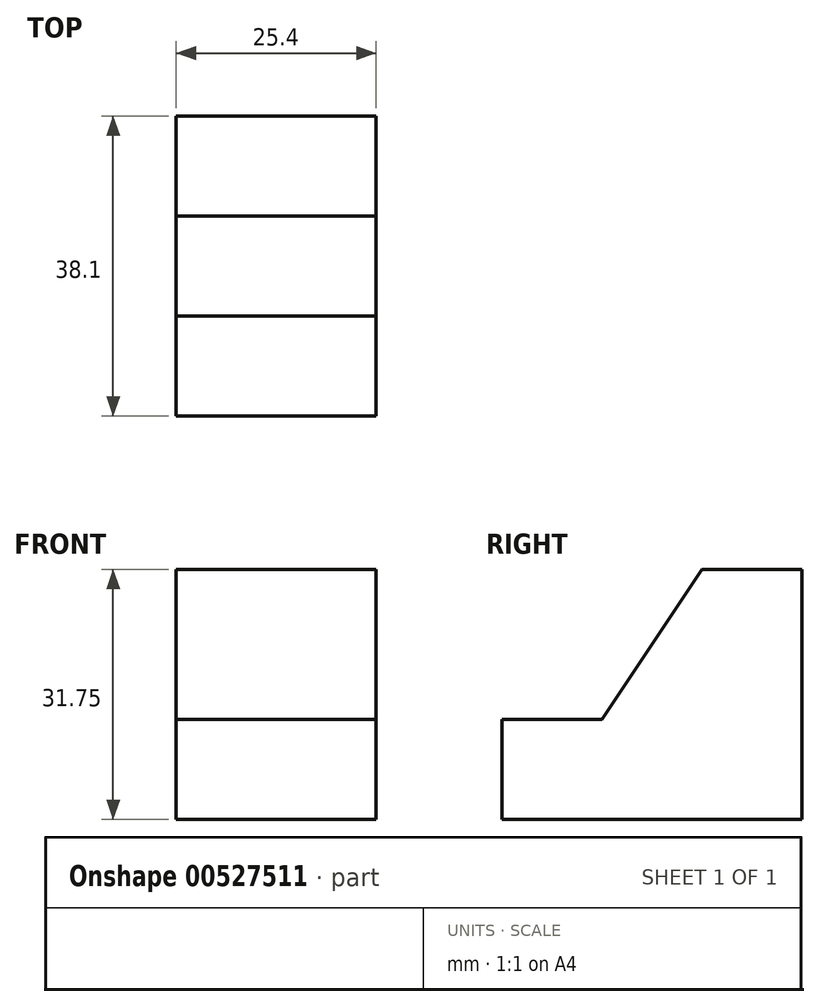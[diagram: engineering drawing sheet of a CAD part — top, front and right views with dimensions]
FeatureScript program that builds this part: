
annotation { "Feature Type Name" : "Feature", "Feature Type Description" : "" }
export const myFeature = defineFeature(function(context is Context, id is Id, definition is map)
    precondition{}
    {
        {
            var Q0;
            Q0=qCreatedBy(makeId("Right.planeOp"),FACE);
            var sketch = newSketch(context, id + "F0", { "sketchPlane" : qUnion([Q0])});
            skLineSegment(sketch, "E0", {"start": v(0, 0) * mm, "end": v(0, 31.75) * mm});
            skLineSegment(sketch, "E1", {"start": v(0, 31.75) * mm, "end": v(-12.7, 31.75) * mm});
            skLineSegment(sketch, "E2", {"start": v(0, 0) * mm, "end": v(-38.1, 0) * mm});
            skLineSegment(sketch, "E3", {"start": v(-38.1, 0) * mm, "end": v(-38.1, 12.7) * mm});
            skLineSegment(sketch, "E4", {"start": v(-38.1, 12.7) * mm, "end": v(-25.4, 12.7) * mm});
            skLineSegment(sketch, "E5", {"start": v(-25.4, 12.7) * mm, "end": v(-12.7, 31.75) * mm});
            skSolve(sketch);
        }
        {
            var Q0;
            Q0=makeQuery(id+"F0.imprint","IMPRINT",FACE,{"disambiguationData":[TD([[makeQuery(id+"F0.imprint","IMPRINT",EDGE,{"derivedFrom":sQuery(id+"F0.wireOp",EDGE,"E0")}),1.0]])]});
            extrude(context, id + "F1", {"entities" : qUnion([Q0]), "depth" : 25.4 * mm, "offsetDistance" : 25.4 * mm});
        }
    });
